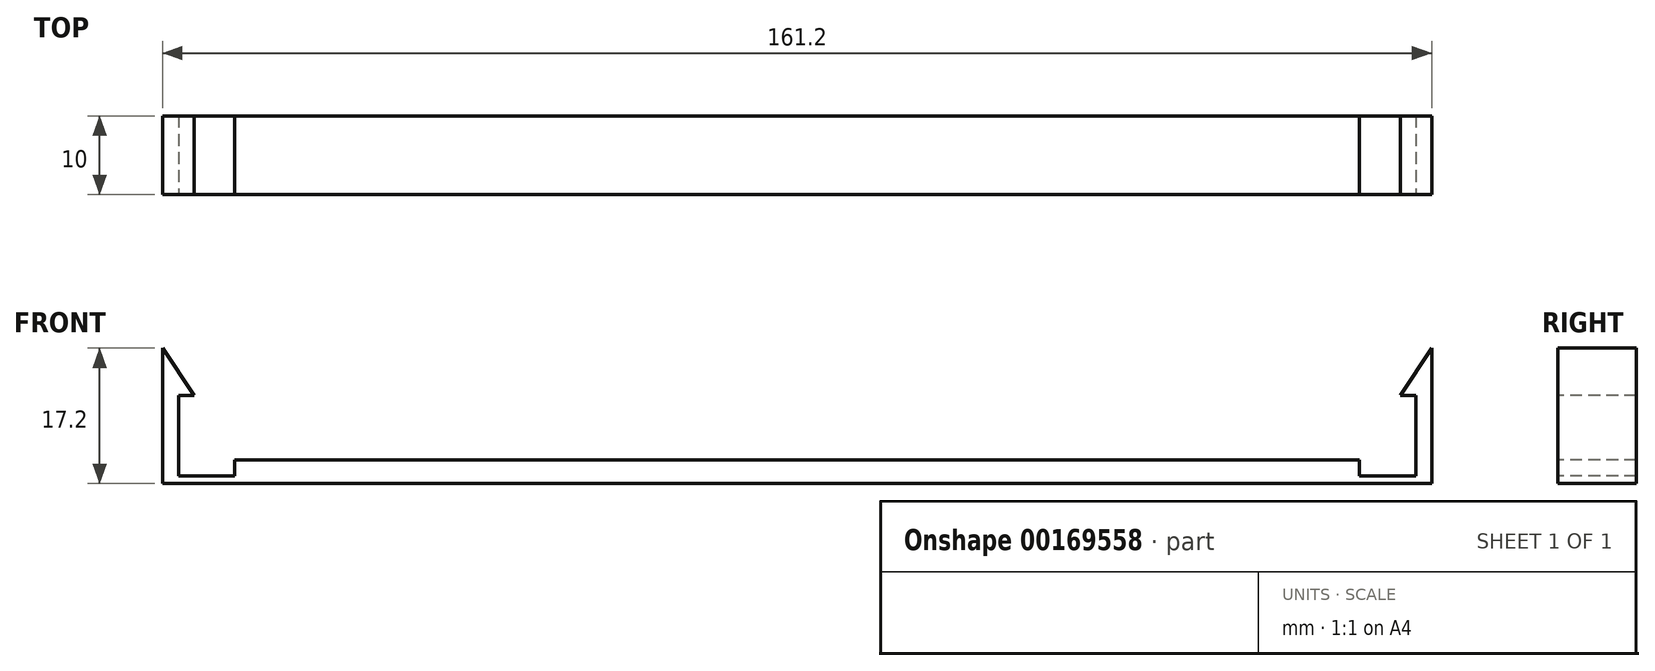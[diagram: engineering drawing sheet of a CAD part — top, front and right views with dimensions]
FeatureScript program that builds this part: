
annotation { "Feature Type Name" : "Feature", "Feature Type Description" : "" }
export const myFeature = defineFeature(function(context is Context, id is Id, definition is map)
    precondition{}
    {
        {
            var Q0;
            Q0=qCreatedBy(makeId("Top.planeOp"),FACE);
            var sketch = newSketch(context, id + "F0", { "sketchPlane" : qUnion([Q0])});
            skLineSegment(sketch, "E0.bottom", {"start": v(80.6, -5) * mm, "end": v(-80.6, -5) * mm});
            skLineSegment(sketch, "E0.top", {"start": v(80.6, 5) * mm, "end": v(-80.6, 5) * mm});
            skLineSegment(sketch, "E0.left", {"start": v(80.6, -5) * mm, "end": v(80.6, 5) * mm});
            skLineSegment(sketch, "E0.right", {"start": v(-80.6, -5) * mm, "end": v(-80.6, 5) * mm});
            skPoint(sketch, "E0.middle", {"position": v(0, 0) * mm});
            skSolve(sketch);
        }
        {
            var Q0;
            Q0 = qSketchRegion(id + "F0", true);
            extrude(context, id + "F1", {"entities" : qUnion([Q0]), "depth" : 1 * mm});
        }
        {
            var Q0;
            Q0=makeQuery(id+"F1.opExtrude","CAP_FACE",FACE,{"disambiguationData":[OSD([sQuery(id+"F0.wireOp",EDGE,"E0.bottom"),sQuery(id+"F0.wireOp",EDGE,"E0.top"),sQuery(id+"F0.wireOp",EDGE,"E0.left"),sQuery(id+"F0.wireOp",EDGE,"E0.right")])],"isStart":false});
            var sketch = newSketch(context, id + "F2", { "sketchPlane" : qUnion([Q0])});
            skLineSegment(sketch, "E1.bottom", {"start": v(-80.6, 5) * mm, "end": v(-78.6, 5) * mm});
            skLineSegment(sketch, "E1.top", {"start": v(-80.6, -5) * mm, "end": v(-78.6, -5) * mm});
            skLineSegment(sketch, "E1.left", {"start": v(-80.6, 5) * mm, "end": v(-80.6, -5) * mm});
            skLineSegment(sketch, "E1.right", {"start": v(-78.6, 5) * mm, "end": v(-78.6, -5) * mm});
            skLineSegment(sketch, "E2.bottom", {"start": v(80.6, 5) * mm, "end": v(78.6, 5) * mm});
            skLineSegment(sketch, "E2.top", {"start": v(80.6, -5) * mm, "end": v(78.6, -5) * mm});
            skLineSegment(sketch, "E2.left", {"start": v(80.6, 5) * mm, "end": v(80.6, -5) * mm});
            skLineSegment(sketch, "E2.right", {"start": v(78.6, 5) * mm, "end": v(78.6, -5) * mm});
            skLineSegment(sketch, "E3.bottom", {"start": v(-71.45, 5) * mm, "end": v(71.45, 5) * mm});
            skLineSegment(sketch, "E3.top", {"start": v(-71.45, -5) * mm, "end": v(71.45, -5) * mm});
            skLineSegment(sketch, "E3.left", {"start": v(-71.45, 5) * mm, "end": v(-71.45, -5) * mm});
            skLineSegment(sketch, "E3.right", {"start": v(71.45, 5) * mm, "end": v(71.45, -5) * mm});
            skSolve(sketch);
        }
        {
            var Q0;
            Q0=makeQuery(id+"F2.imprint","IMPRINT",FACE,{"disambiguationData":[TD([[makeQuery(id+"F2.imprint","IMPRINT",EDGE,{"derivedFrom":sQuery(id+"F2.wireOp",EDGE,"E1.bottom")}),1.0]])]});
            var Q1;
            Q1=makeQuery(id+"F2.imprint","IMPRINT",FACE,{"disambiguationData":[TD([[makeQuery(id+"F2.imprint","IMPRINT",EDGE,{"derivedFrom":sQuery(id+"F2.wireOp",EDGE,"E2.bottom")}),1.0]])]});
            extrude(context, id + "F3", {"entities" : qUnion([Q0, Q1]), "operationType" : NewBodyOperationType.ADD, "depth" : 10.2 * mm});
        }
        {
            var Q0;
            Q0=makeQuery(id+"F2.imprint","IMPRINT",FACE,{"disambiguationData":[TD([[makeQuery(id+"F2.imprint","IMPRINT",EDGE,{"derivedFrom":sQuery(id+"F2.wireOp",EDGE,"E3.bottom")}),1.0]])]});
            extrude(context, id + "F4", {"entities" : qUnion([Q0]), "operationType" : NewBodyOperationType.ADD, "depth" : 2 * mm});
        }
        {
            var Q0;
            Q0=makeQuery(id+"F4.boolean.opBoolean","MERGE",FACE,{"derivedFrom":[makeQuery(id+"F3.boolean.opBoolean","MERGE",FACE,{"derivedFrom":[makeQuery(id+"F1.opExtrude","SWEPT_FACE",FACE,{"disambiguationData":[OSD([sQuery(id+"F0.wireOp",EDGE,"E0.bottom")])]}),makeQuery(id+"F3.opExtrude","SWEPT_FACE",FACE,{"disambiguationData":[OSD([sQuery(id+"F2.wireOp",EDGE,"E1.top")])]}),makeQuery(id+"F3.opExtrude","SWEPT_FACE",FACE,{"disambiguationData":[OSD([sQuery(id+"F2.wireOp",EDGE,"E2.top")])]})]}),makeQuery(id+"F4.opExtrude","SWEPT_FACE",FACE,{"disambiguationData":[OSD([sQuery(id+"F2.wireOp",EDGE,"E3.top")])]})]});
            var sketch = newSketch(context, id + "F5", { "sketchPlane" : qUnion([Q0])});
            skLineSegment(sketch, "E4", {"start": v(-80.6, 17.2) * mm, "end": v(-80.6, 11.2) * mm});
            skLineSegment(sketch, "E5", {"start": v(-80.6, 11.2) * mm, "end": v(-76.6, 11.2) * mm});
            skLineSegment(sketch, "E6", {"start": v(-76.6, 11.2) * mm, "end": v(-80.6, 17.2) * mm});
            skLineSegment(sketch, "E7", {"start": v(80.6, 17.2) * mm, "end": v(80.6, 11.2) * mm});
            skLineSegment(sketch, "E8.MirrorCS", {"start": v(76.6, 11.2) * mm, "end": v(80.6, 17.2) * mm});
            skLineSegment(sketch, "E9.MirrorCS", {"start": v(80.6, 11.2) * mm, "end": v(76.6, 11.2) * mm});
            skSolve(sketch);
        }
        {
            var Q0;
            {var subQ3=sQuery(id+"F5.wireOp",EDGE,"E8.MirrorCS");Q0=makeQuery(id+"F5.imprint","IMPRINT",FACE,{"disambiguationData":[TD([[makeQuery(id+"F5.imprint","IMPRINT",EDGE,{"derivedFrom":subQ3}),-1.0]])]});}
            var Q1;
            {var subQ0=sQuery(id+"F5.wireOp",EDGE,"E4");Q1=makeQuery(id+"F5.imprint","IMPRINT",FACE,{"disambiguationData":[TD([[makeQuery(id+"F5.imprint","IMPRINT",EDGE,{"derivedFrom":subQ0}),1.0]])]});}
            extrude(context, id + "F6", {"entities" : qUnion([Q0, Q1]), "operationType" : NewBodyOperationType.ADD, "oppositeDirection" : true, "depth" : 10 * mm});
        }
    });
